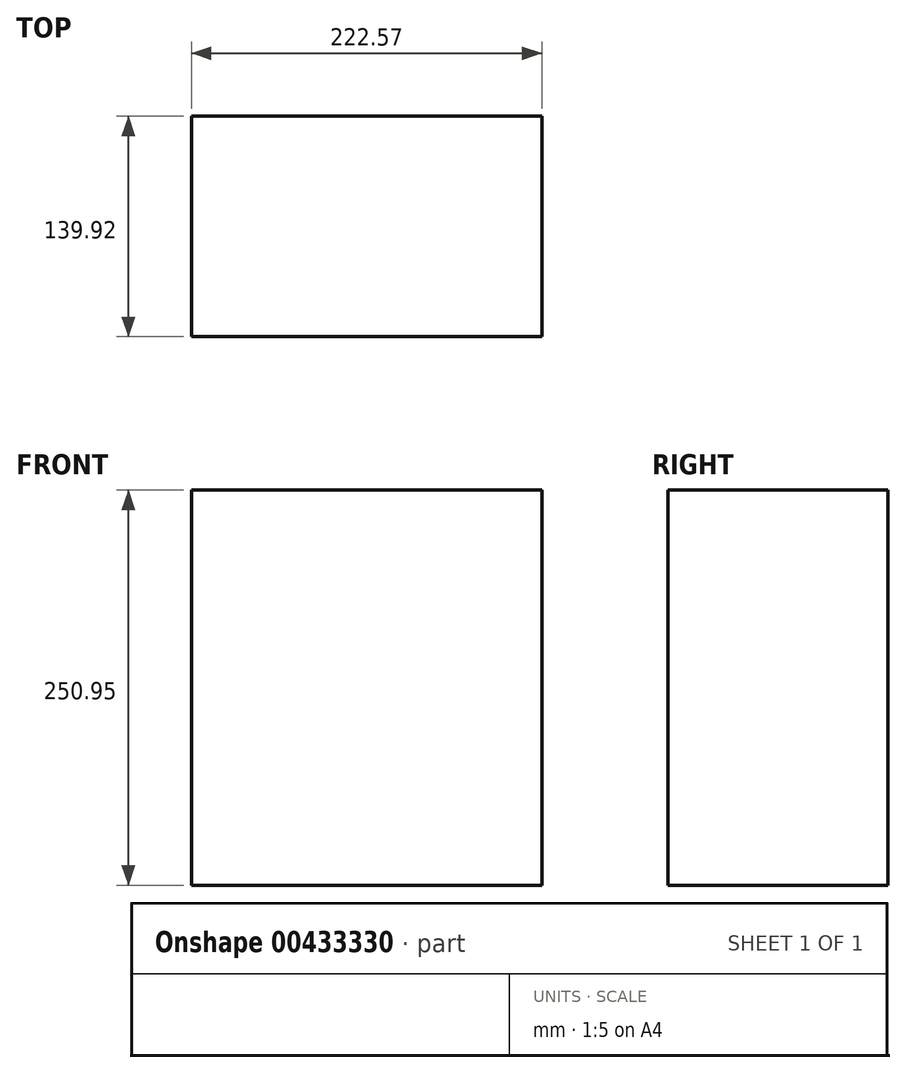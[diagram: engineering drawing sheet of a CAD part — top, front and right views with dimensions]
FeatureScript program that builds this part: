
annotation { "Feature Type Name" : "Feature", "Feature Type Description" : "" }
export const myFeature = defineFeature(function(context is Context, id is Id, definition is map)
    precondition{}
    {
        {
            var Q0;
            Q0=qCreatedBy(makeId("Top.planeOp"),FACE);
            var sketch = newSketch(context, id + "F0", { "sketchPlane" : qUnion([Q0])});
            skLineSegment(sketch, "E0.bottom", {"start": v(-102.61, 55.5) * mm, "end": v(119.96, 55.5) * mm});
            skLineSegment(sketch, "E0.top", {"start": v(-102.61, -84.4) * mm, "end": v(119.96, -84.4) * mm});
            skLineSegment(sketch, "E0.left", {"start": v(-102.61, 55.5) * mm, "end": v(-102.61, -84.4) * mm});
            skLineSegment(sketch, "E0.right", {"start": v(119.96, 55.5) * mm, "end": v(119.96, -84.4) * mm});
            skSolve(sketch);
        }
        {
            var Q0;
            Q0=makeQuery(id+"F0.imprint","IMPRINT",FACE,{"disambiguationData":[TD([[makeQuery(id+"F0.imprint","IMPRINT",EDGE,{"derivedFrom":sQuery(id+"F0.wireOp",EDGE,"E0.bottom")}),-1.0]])]});
            extrude(context, id + "F1", {"entities" : qUnion([Q0]), "depth" : 250.95 * mm});
        }
    });
